# Revit family: OPAL CARE STANDARD HANDLE W-C
name_source: partatom
category: Specialty Equipment
units: mm (PartAtom-declared; Revit-internal decimal feet)

## family parameters
Cut with Voids When Loaded = No
Host = Face
OmniClass Number = 23.45.55.14
OmniClass Title = Single Faucets
Part Type = Normal
Room Calculation Point = No
Round Connector Dimension = Use Radius
Shared = No

## types (3) — shared parameters
Assembly Code = C1030220
Default Elevation = 1000 mm
Manufacturer = GWA Bathrooms & Kitchens
URL = https://www.caroma.com.au

## per-type parameters (varying)
| type | Material_Base | Model |
| OPAL CARE STANDARD HANDLE CHROME W-C | GWA_Metal-Chrome | 99703C |
| OPAL CARE STANDARD HANDLE BLACK W-C | GWA-Metal-Black | 99703B |
| OPAL CARE STANDARD HANDLE BRUSHED NICKEL W-C | GWA_Metal-Brushed-Nickel | 99703BN |

note: column(s) folded — value = type name in every type: Description

## geometry (parser evidence)
native form markers: Sweep x2
no freeform markers — native parametric forms only
